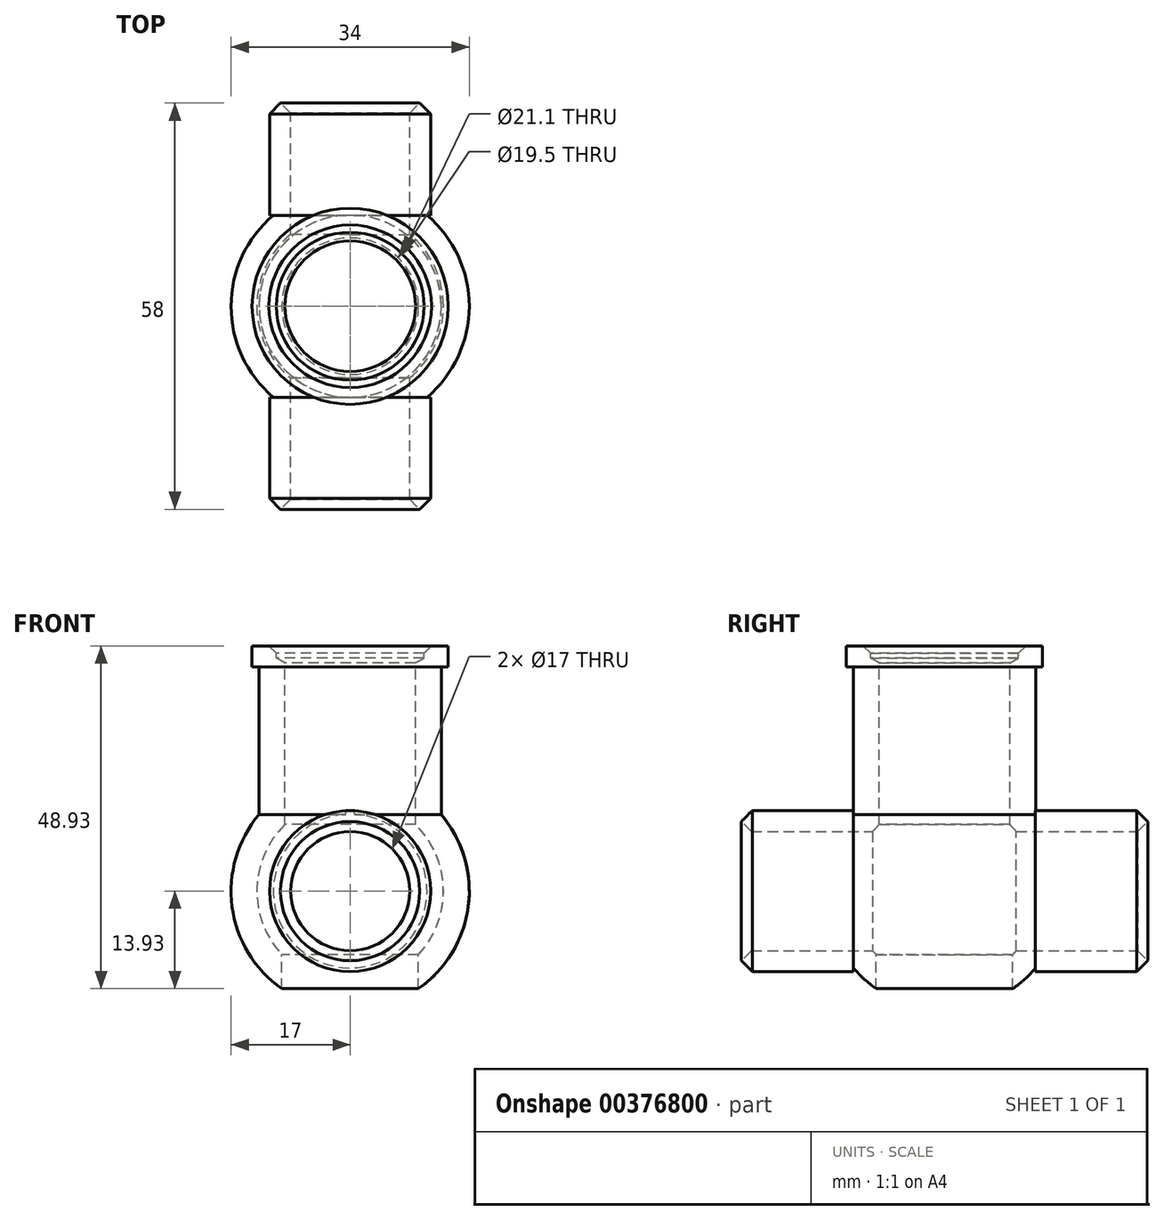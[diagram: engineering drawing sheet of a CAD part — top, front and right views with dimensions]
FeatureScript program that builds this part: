
annotation { "Feature Type Name" : "Feature", "Feature Type Description" : "" }
export const myFeature = defineFeature(function(context is Context, id is Id, definition is map)
    precondition{}
    {
        {
            var Q0;
            Q0=qCreatedBy(makeId("Front.planeOp"),FACE);
            var sketch = newSketch(context, id + "F0", { "sketchPlane" : qUnion([Q0])});
            skArc(sketch, "E0", {"start": v(-9.32, 14.22) * mm, "mid": v(-17, 0.26) * mm, "end": v(-9.75, -13.93) * mm});
            skLineSegment(sketch, "E1", {"start": v(0, 35) * mm, "end": v(0, -13.32) * mm, "construction": true});
            skLineSegment(sketch, "E2", {"start": v(0, 35) * mm, "end": v(-14, 35) * mm});
            skLineSegment(sketch, "E3", {"start": v(-14, 35) * mm, "end": v(-14, 32) * mm});
            skLineSegment(sketch, "E4", {"start": v(-14, 32) * mm, "end": v(-13, 32) * mm});
            skLineSegment(sketch, "E5", {"start": v(-13, 32) * mm, "end": v(-13, 10.95) * mm});
            skLineSegment(sketch, "E6", {"start": v(0, 35) * mm, "end": v(-11.6, 35) * mm});
            skLineSegment(sketch, "E7", {"start": v(-11.6, 35) * mm, "end": v(-10.55, 33.95) * mm});
            skLineSegment(sketch, "E8", {"start": v(-10.55, 33.95) * mm, "end": v(-10.55, 33.25) * mm});
            skLineSegment(sketch, "E9", {"start": v(-10.55, 33.95) * mm, "end": v(0, 33.95) * mm});
            skLineSegment(sketch, "E10", {"start": v(-10.55, 33.25) * mm, "end": v(0, 33.25) * mm});
            skLineSegment(sketch, "E11", {"start": v(0, 32.6) * mm, "end": v(-9.32, 32.6) * mm});
            skLineSegment(sketch, "E12", {"start": v(-10.55, 33.25) * mm, "end": v(-9.32, 32.6) * mm});
            skLineSegment(sketch, "E13", {"start": v(-9.32, 32.6) * mm, "end": v(-9.32, 9.52) * mm});
            skArc(sketch, "E14", {"start": v(-9.32, 9.52) * mm, "mid": v(-13.31, 0.31) * mm, "end": v(-9.75, -9.07) * mm});
            skLineSegment(sketch, "E15", {"start": v(-10.48, 33.21) * mm, "end": v(-10.48, 19.21) * mm});
            skLineSegment(sketch, "E16", {"start": v(-10.48, 19.21) * mm, "end": v(0, 19.21) * mm});
            skLineSegment(sketch, "E17", {"start": v(0, 13.32) * mm, "end": v(0, 17) * mm});
            skLineSegment(sketch, "E18", {"start": v(-9.75, -9.07) * mm, "end": v(-9.75, -13.93) * mm});
            skLineSegment(sketch, "E19.trimOffspring", {"start": v(0, -17) * mm, "end": v(0, -57.86) * mm, "construction": true});
            skSolve(sketch);
        }
        {
            var Q0;
            Q0=qCreatedBy(makeId("Right.planeOp"),FACE);
            var sketch = newSketch(context, id + "F1", { "sketchPlane" : qUnion([Q0])});
            skLineSegment(sketch, "E20", {"start": v(29, 0) * mm, "end": v(-20.36, 0) * mm, "construction": true});
            skLineSegment(sketch, "E21", {"start": v(29, 0) * mm, "end": v(29, 11.5) * mm});
            skLineSegment(sketch, "E22", {"start": v(29, 0) * mm, "end": v(29, -11.5) * mm});
            skLineSegment(sketch, "E23", {"start": v(29, -11.5) * mm, "end": v(0, -11.5) * mm});
            skLineSegment(sketch, "E24", {"start": v(29, 0) * mm, "end": v(29, 8.5) * mm});
            skLineSegment(sketch, "E25", {"start": v(29, 9.93) * mm, "end": v(27.57, 8.5) * mm});
            skLineSegment(sketch, "E26", {"start": v(29, 9.93) * mm, "end": v(27.43, 11.5) * mm});
            skLineSegment(sketch, "E27", {"start": v(27.43, 11.5) * mm, "end": v(0, 11.5) * mm});
            skLineSegment(sketch, "E28", {"start": v(27.57, 8.5) * mm, "end": v(0, 8.5) * mm});
            skLineSegment(sketch, "E29", {"start": v(12.99, 11.5) * mm, "end": v(12.99, 10.97) * mm});
            skArc(sketch, "E30", {"start": v(12.99, 10.97) * mm, "mid": v(13.9, 9.77) * mm, "end": v(14.72, 8.5) * mm});
            skPoint(sketch, "E31", {"position": v(17, 0) * mm});
            skArc(sketch, "E32.MirrorCS", {"start": v(-12.99, 10.97) * mm, "mid": v(-13.9, 9.77) * mm, "end": v(-14.72, 8.5) * mm});
            skLineSegment(sketch, "E33.MirrorCS", {"start": v(-27.43, 11.5) * mm, "end": v(0, 11.5) * mm});
            skLineSegment(sketch, "E34.MirrorCS", {"start": v(-12.99, 11.5) * mm, "end": v(-12.99, 10.97) * mm});
            skLineSegment(sketch, "E35.MirrorCS", {"start": v(-27.57, 8.5) * mm, "end": v(0, 8.5) * mm});
            skLineSegment(sketch, "E36.MirrorCS", {"start": v(-29, 9.93) * mm, "end": v(-27.57, 8.5) * mm});
            skLineSegment(sketch, "E37.MirrorCS", {"start": v(-29, 9.93) * mm, "end": v(-27.43, 11.5) * mm});
            skPoint(sketch, "E38", {"position": v(-20.36, 0) * mm});
            skSolve(sketch);
        }
        {
            var Q0;
            Q0 = qSketchRegion(id + "F0", true);
            var Q1;
            Q1=sQuery(id+"F0.wireOp",EDGE,"E1");
            revolve(context, id + "F2", {"entities" : qUnion([Q0]), "axis" : qUnion([Q1]), "revolveType" : RevolveType.FULL});
        }
        {
            var Q0;
            {var subQ1=sQuery(id+"F1.wireOp",EDGE,"E25");Q0=makeQuery(id+"F1.imprint","IMPRINT",FACE,{"disambiguationData":[TD([[makeQuery(id+"F1.imprint","IMPRINT",EDGE,{"derivedFrom":subQ1}),-1.0]])]});}
            var Q1;
            Q1=sQuery(id+"F1.wireOp",EDGE,"E20");
            revolve(context, id + "F3", {"operationType" : NewBodyOperationType.ADD, "entities" : qUnion([Q0]), "axis" : qUnion([Q1]), "revolveType" : RevolveType.FULL});
        }
        {
            var Q0;
            {var subQ1=sQuery(id+"F1.wireOp",EDGE,"E32.MirrorCS");Q0=makeQuery(id+"F1.imprint","IMPRINT",FACE,{"disambiguationData":[TD([[makeQuery(id+"F1.imprint","IMPRINT",EDGE,{"derivedFrom":subQ1}),-1.0]])]});}
            var Q1;
            Q1=sQuery(id+"F1.wireOp",EDGE,"E20");
            revolve(context, id + "F4", {"operationType" : NewBodyOperationType.ADD, "entities" : qUnion([Q0]), "axis" : qUnion([Q1]), "revolveType" : RevolveType.FULL});
        }
        {
            var Q0;
            Q0=sQuery(id+"F0.wireOp",VERTEX,"E14.center");
            var Q1;
            Q1=makeQuery(id+"F2.opRevolve","SWEPT_BODY",BODY,{"disambiguationData":[OSD([sQuery(id+"F0.wireOp",EDGE,"E0"),sQuery(id+"F0.wireOp",EDGE,"E2"),sQuery(id+"F0.wireOp",EDGE,"E3"),sQuery(id+"F0.wireOp",EDGE,"E4"),sQuery(id+"F0.wireOp",EDGE,"E5"),sQuery(id+"F0.wireOp",EDGE,"E7"),sQuery(id+"F0.wireOp",EDGE,"E8"),sQuery(id+"F0.wireOp",EDGE,"E12"),sQuery(id+"F0.wireOp",EDGE,"E13"),sQuery(id+"F0.wireOp",EDGE,"E14"),sQuery(id+"F0.wireOp",EDGE,"E18")])]});
            hole(context, id + "F5", {"style" : HoleStyle.SIMPLE, "endStyle" : HoleEndStyle.BLIND, "oppositeDirection" : true, "holeDiameter" : 17 * mm, "holeDepth" : 29 * mm, "isTappedThrough" : true, "tappedDepth" : 12 * mm, "tapClearance" : 3, "startFromSketch" : true, "locations" : qUnion([Q0]), "scope" : qUnion([Q1])});
        }
        {
            var Q0;
            Q0=sQuery(id+"F0.wireOp",VERTEX,"E14.center");
            var Q1;
            Q1=makeQuery(id+"F2.opRevolve","SWEPT_BODY",BODY,{"disambiguationData":[OSD([sQuery(id+"F0.wireOp",EDGE,"E0"),sQuery(id+"F0.wireOp",EDGE,"E2"),sQuery(id+"F0.wireOp",EDGE,"E3"),sQuery(id+"F0.wireOp",EDGE,"E4"),sQuery(id+"F0.wireOp",EDGE,"E5"),sQuery(id+"F0.wireOp",EDGE,"E7"),sQuery(id+"F0.wireOp",EDGE,"E8"),sQuery(id+"F0.wireOp",EDGE,"E12"),sQuery(id+"F0.wireOp",EDGE,"E13"),sQuery(id+"F0.wireOp",EDGE,"E14"),sQuery(id+"F0.wireOp",EDGE,"E18")])]});
            hole(context, id + "F6", {"style" : HoleStyle.SIMPLE, "endStyle" : HoleEndStyle.BLIND, "holeDiameter" : 17 * mm, "holeDepth" : 29 * mm, "isTappedThrough" : true, "tappedDepth" : 12 * mm, "tapClearance" : 3, "startFromSketch" : true, "locations" : qUnion([Q0]), "scope" : qUnion([Q1])});
        }
    });
